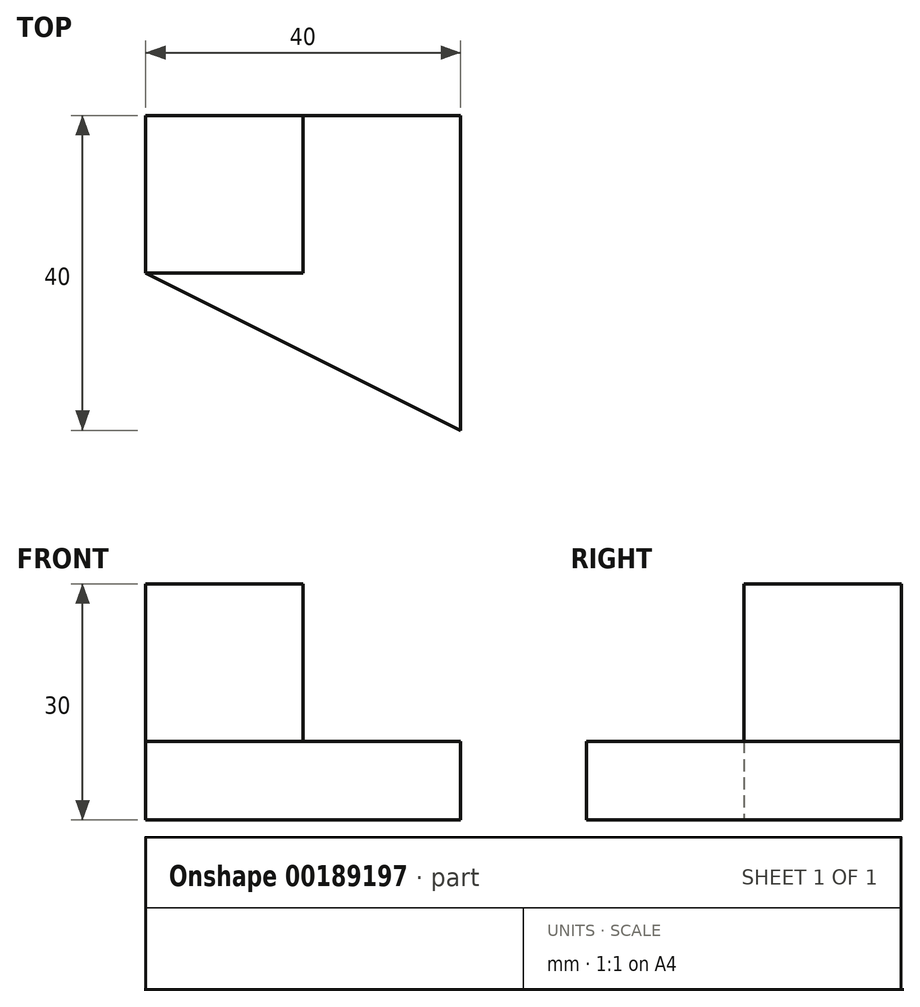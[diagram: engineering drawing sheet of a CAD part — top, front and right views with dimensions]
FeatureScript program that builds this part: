
annotation { "Feature Type Name" : "Feature", "Feature Type Description" : "" }
export const myFeature = defineFeature(function(context is Context, id is Id, definition is map)
    precondition{}
    {
        {
            var Q0;
            Q0=qCreatedBy(makeId("Top.planeOp"),FACE);
            var sketch = newSketch(context, id + "F0", { "sketchPlane" : qUnion([Q0])});
            skLineSegment(sketch, "E0", {"start": v(0, 0) * mm, "end": v(0, 40) * mm});
            skLineSegment(sketch, "E1", {"start": v(0, 40) * mm, "end": v(-40, 40) * mm});
            skLineSegment(sketch, "E2", {"start": v(-40, 40) * mm, "end": v(-40, 20) * mm});
            skLineSegment(sketch, "E3", {"start": v(-40, 20) * mm, "end": v(0, 0) * mm});
            skSolve(sketch);
        }
        {
            var Q0;
            Q0=makeQuery(id+"F0.imprint","IMPRINT",FACE,{"disambiguationData":[TD([[makeQuery(id+"F0.imprint","IMPRINT",EDGE,{"derivedFrom":sQuery(id+"F0.wireOp",EDGE,"E0")}),1.0]])]});
            extrude(context, id + "F1", {"entities" : qUnion([Q0]), "depth" : 10 * mm});
        }
        {
            var Q0;
            Q0=makeQuery(id+"F1.opExtrude","CAP_FACE",FACE,{"disambiguationData":[OSD([sQuery(id+"F0.wireOp",EDGE,"E0"),sQuery(id+"F0.wireOp",EDGE,"E1"),sQuery(id+"F0.wireOp",EDGE,"E2"),sQuery(id+"F0.wireOp",EDGE,"E3")])],"isStart":false});
            var sketch = newSketch(context, id + "F2", { "sketchPlane" : qUnion([Q0])});
            skLineSegment(sketch, "E4.bottom", {"start": v(-40, 40) * mm, "end": v(-20, 40) * mm});
            skLineSegment(sketch, "E4.top", {"start": v(-40, 20) * mm, "end": v(-20, 20) * mm});
            skLineSegment(sketch, "E4.left", {"start": v(-40, 40) * mm, "end": v(-40, 20) * mm});
            skLineSegment(sketch, "E4.right", {"start": v(-20, 40) * mm, "end": v(-20, 20) * mm});
            skSolve(sketch);
        }
        {
            var Q0;
            Q0=makeQuery(id+"F2.imprint","IMPRINT",FACE,{"disambiguationData":[TD([[makeQuery(id+"F2.imprint","IMPRINT",EDGE,{"derivedFrom":sQuery(id+"F2.wireOp",EDGE,"E4.bottom")}),1.0]])]});
            extrude(context, id + "F3", {"entities" : qUnion([Q0]), "operationType" : NewBodyOperationType.ADD, "depth" : 20 * mm});
        }
    });
